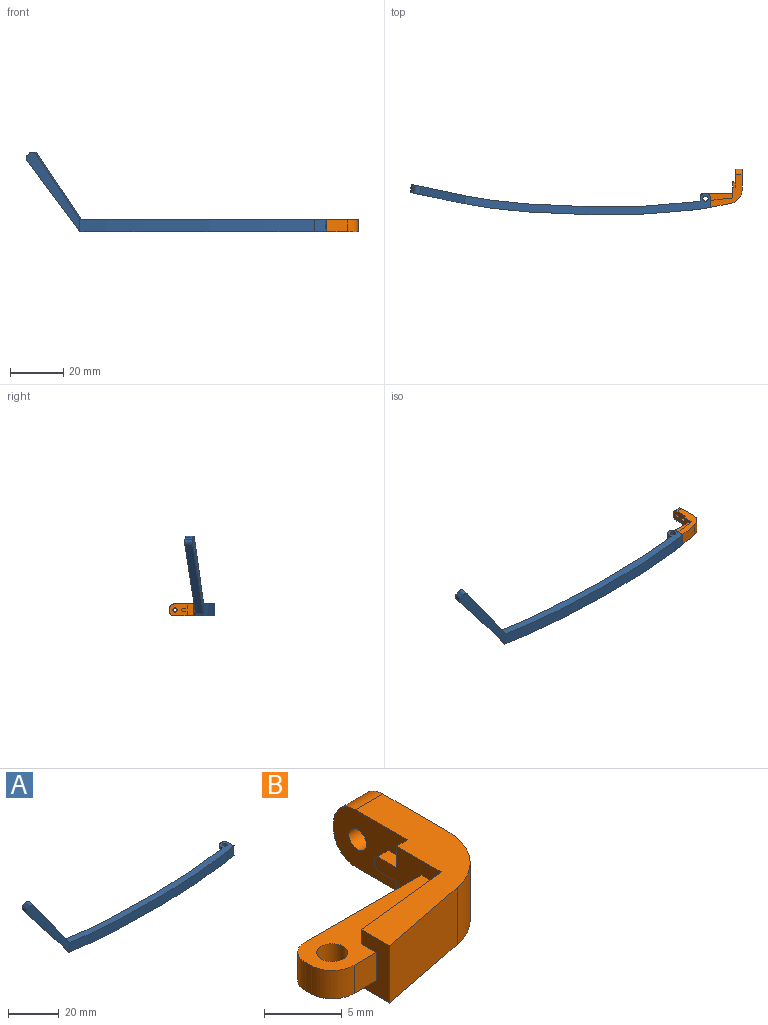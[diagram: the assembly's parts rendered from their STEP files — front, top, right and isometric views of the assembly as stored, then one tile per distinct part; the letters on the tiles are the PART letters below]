
ASSEMBLY  parts=2 mates=1
PART A: 32 faces, bbox 112.7x11.7x29.9 mm
  f0: plane 1.14x0.02mm, normal (-0.11,0.99,0), area 0mm2, adj f9,f28
  f1: plane 1.14x0.02mm, normal (-0.11,0.99,0), area 0mm2, adj f6,f30
  f2: plane 5.28x4.01mm, normal (0,0,1), area 12.2mm2, adj f5,f6,f7,f8,f26,f27,f30
  f3: plane 5.28x4.01mm, normal (0,0,-1), area 12.2mm2, adj f5,f9,f11,f12,f26,f27,f28
  f4: plane 92.4x9.36mm, normal (0,0,1), area 280mm2, adj f5,f9,f11,f12,f13,f14,f16,f19
  f5: plane 4.5x4.5mm, normal (0.19,-0.98,0), area 19.9mm2, adj f2,f3,f4,f10,f16,f27,f28,f29
  f6: cylinder r=2mm len=4mm, axis (0,0,1), area 7.9mm2, adj f1,f2,f7,f10
  f7: plane 1.14x1.09mm, normal (-1,0.01,0), area 1.2mm2, adj f2,f6,f10,f13
  f8: cylinder r=1mm len=2mm, axis (0,0,1), area 7.1mm2, adj f2,f10
  f9: cylinder r=2mm len=4mm, axis (0,0,1), area 7.9mm2, adj f0,f3,f4,f11
  f10: plane 92.74x11.18mm, normal (0,0,-1), area 281.1mm2, adj f5,f6,f7,f8,f13,f14,f15,f16
  f11: plane 1.14x1.09mm, normal (-1,0.01,0), area 1.2mm2, adj f3,f4,f9,f13
  f12: cylinder r=1mm len=2mm, axis (0,0,1), area 7.1mm2, adj f3,f4
  f13: plane 4.5x1.07mm, normal (-0.11,0.99,0), area 4.8mm2, adj f4,f7,f10,f11,f14,f26
  f14: bspline ~86.85x4.5mm, area 391.9mm2, adj f4,f10,f13,f20
  f15: bspline ~21.71x4.5mm, area 0.2mm2, adj f10,f17,f25
  f16: bspline ~87.9x4.5mm, area 396.9mm2, adj f4,f5,f10,f22
  f17: plane 26.76x20.54mm, normal (-0.78,0.14,-0.6), area 97.7mm2, adj f15,f20,f21,f22,f24,f25
  f18: plane 3.11x1.39mm, normal (-0.65,0.12,0.75), area 3.5mm2, adj f21,f22,f23,f24
  f19: plane 24.79x17.29mm, normal (0.81,-0.15,0.57), area 90.2mm2, adj f4,f20,f21,f22,f23
  f20: plane 4.5x0.03mm, normal (0.98,-0.18,0), area 0.1mm2, adj f14,f17,f19,f21
  f21: plane 29.94x20.31mm, normal (0.18,0.98,0), area 113.7mm2, adj f17,f18,f19,f20,f23,f24
  f22: plane 29.94x20.31mm, normal (-0.18,-0.98,0), area 113.8mm2, adj f10,f16,f17,f18,f19,f23,f24,f25
  f23: cylinder r=1.5mm len=3.35mm, axis (-0.18,-0.98,0), area 7.6mm2, adj f18,f19,f21,f22
  f24: cylinder r=1.5mm len=3.04mm, axis (0.18,0.98,0), area 6.7mm2, adj f17,f18,f21,f22
  f25: plane 3x0.87mm, normal (-0.93,0.16,-0.32), area 2.6mm2, adj f10,f15,f17,f22
  f26: cylinder r=2.28mm len=2.47mm, axis (0,0,-1), area 6.5mm2, adj f2,f3,f13,f27
  f27: plane 2.23x1.28mm, normal (0.63,0.78,0), area 3.7mm2, adj f2,f3,f5,f26
  f28: plane 2.61x1.14mm, normal (1,0,0), area 3mm2, adj f0,f3,f4,f5,f29
  f29: plane 0.09x0.04mm, normal (0,0.91,-0.42), area 0mm2, adj f4,f5,f28
  f30: plane 2.6x1.14mm, normal (1,0,0), area 3mm2, adj f1,f2,f5,f10,f31
  f31: plane 0.09x0.04mm, normal (0,0.91,0.42), area 0mm2, adj f5,f10,f30
PART B: 29 faces, bbox 15.7x14.3x4.5 mm
  f0: plane 6.1x4.5mm, normal (-1,0,0), area 16.4mm2, adj f1,f2,f3,f4,f5,f6,f9,f18
  f1: plane 1x0.5mm, normal (0,1,0), area 0.5mm2, adj f0,f17,f27,f28
  f2: plane 12.3x11.7mm, normal (0,0,-1), area 46.5mm2, adj f0,f7,f9,f10,f11,f15,f16,f17
  f3: plane 12.3x11.7mm, normal (0,0,1), area 46.5mm2, adj f0,f7,f10,f11,f14,f15,f17,f18
  f4: plane 10.6x2.23mm, normal (0,1,0), area 23.6mm2, adj f0,f5,f6,f26
  f5: plane 12.2x4.08mm, normal (0,0,-1), area 30.2mm2, adj f0,f4,f8,f9,f10,f19,f20,f21
  f6: plane 12.2x4.08mm, normal (0,0,1), area 30.2mm2, adj f0,f4,f8,f10,f18,f19,f20,f21
  f7: plane 7.66x4.5mm, normal (0.19,-0.98,0), area 35.2mm2, adj f2,f3,f10,f11
  f8: plane 2.23x0.57mm, normal (-1,0,0), area 1.3mm2, adj f5,f6,f21,f26
  f9: plane 8.2x1.14mm, normal (-0.11,0.99,0), area 9.4mm2, adj f0,f2,f5,f10
  f10: plane 4.5x2.59mm, normal (-1,0,0), area 8.6mm2, adj f2,f3,f5,f6,f7,f9,f18,f20
  f11: cylinder r=5mm len=4.91mm, axis (0,0,-1), area 31mm2, adj f2,f3,f7,f15
  f12: plane 2.5x0.5mm, normal (0,1,0), area 1.3mm2, adj f14,f15,f16,f17
  f13: cylinder r=0.8mm len=2.5mm, axis (-1,0,0), area 12.6mm2, adj f15,f17
  f14: cylinder r=2mm len=2.5mm, axis (1,0,0), area 7.9mm2, adj f3,f12,f15,f17
  f15: plane 7.89x4.5mm, normal (1,0,0), area 31.8mm2, adj f2,f3,f11,f12,f13,f14,f16
  f16: cylinder r=2mm len=2.5mm, axis (-1,0,0), area 7.9mm2, adj f2,f12,f15,f17
  f17: plane 6.75x4.5mm, normal (-1,0,0), area 24.5mm2, adj f1,f2,f3,f12,f13,f14,f16,f22
  f18: plane 8.2x1.14mm, normal (-0.11,0.99,0), area 9.4mm2, adj f0,f3,f6,f10
  f19: cylinder r=1mm len=2.23mm, axis (0,0,1), area 14mm2, adj f5,f6
  f20: plane 2.23x2mm, normal (0,-1,0), area 4.5mm2, adj f5,f6,f10,f21
  f21: cylinder r=2mm len=2.23mm, axis (0,0,1), area 6.8mm2, adj f5,f6,f8,f20
  f22: plane 1.75x1mm, normal (0,0,1), area 1.8mm2, adj f0,f17,f23,f28
  f23: plane 1.7x1mm, normal (0,1,0), area 1.7mm2, adj f0,f3,f17,f22
  f24: plane 1.75x1mm, normal (0,0,-1), area 1.8mm2, adj f0,f17,f25,f27
  f25: plane 1.7x1mm, normal (0,1,0), area 1.7mm2, adj f0,f2,f17,f24
  f26: cylinder r=1.6mm len=2.23mm, axis (0,0,-1), area 5.6mm2, adj f4,f5,f6,f8
  f27: plane 1x0.3mm, normal (0,0.71,-0.71), area 0.4mm2, adj f0,f1,f17,f24
  f28: plane 1x0.3mm, normal (0,0.71,0.71), area 0.4mm2, adj f0,f1,f17,f22
PLACE A rot(axis=(0,0,-1),1.4deg) t=(9.52,-18.61,21.98)mm
PLACE B t=(9.56,-17,21.98)mm fixed
MATE revolute A.f6 <-> B.f19  axis (0,0,-1) through (-54.88,-16.08,25.35)mm
